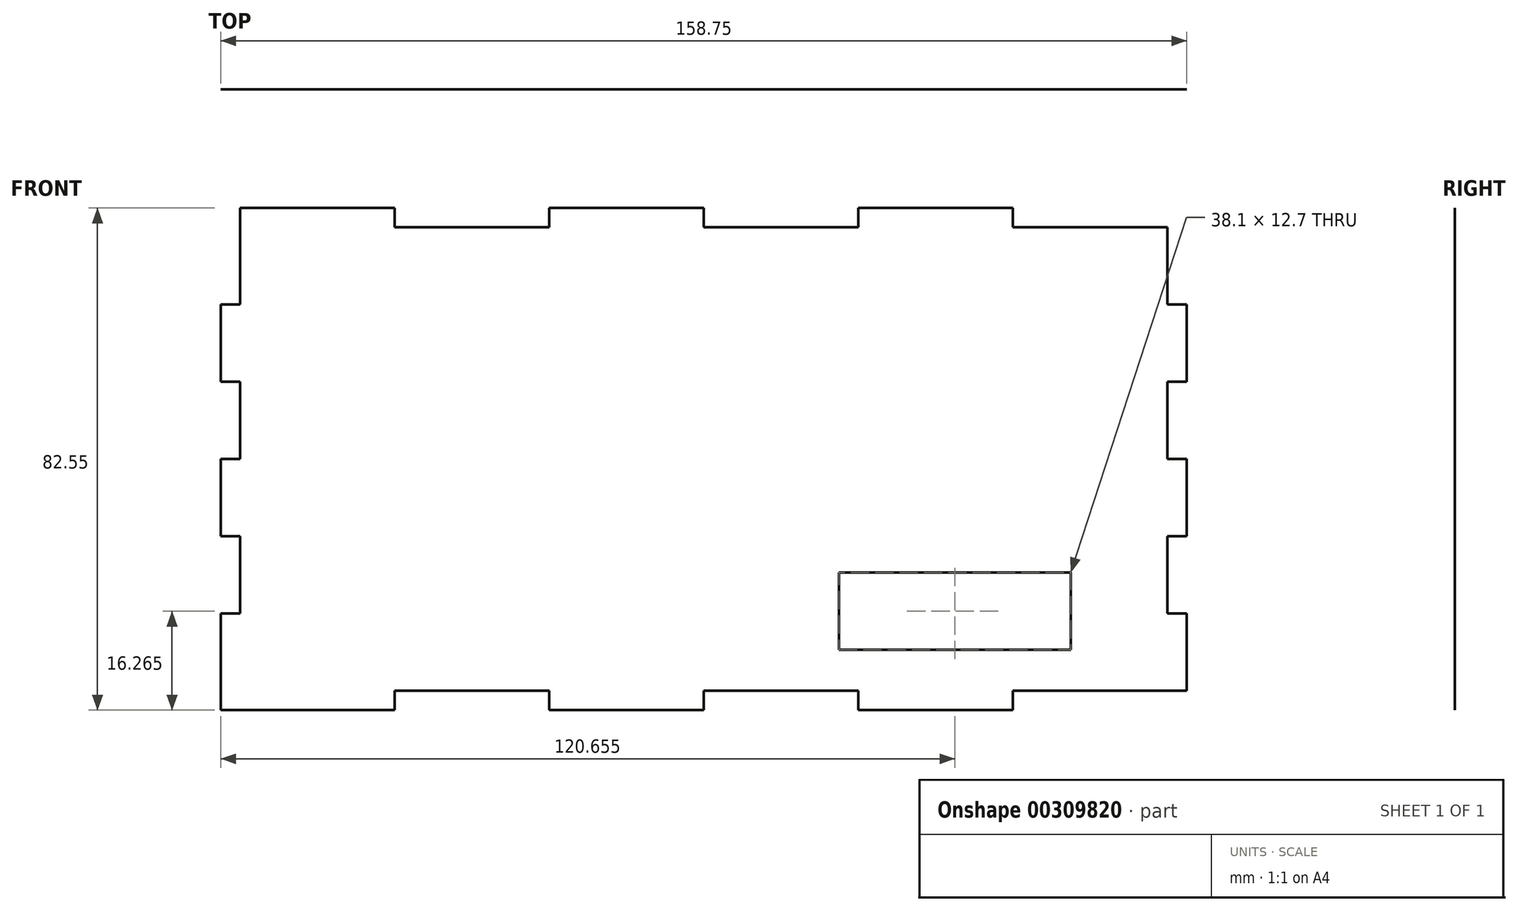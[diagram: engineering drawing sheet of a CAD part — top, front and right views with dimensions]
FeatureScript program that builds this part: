
annotation { "Feature Type Name" : "Feature", "Feature Type Description" : "" }
export const myFeature = defineFeature(function(context is Context, id is Id, definition is map)
    precondition{}
    {
        {
            var Q0;
            Q0=qCreatedBy(makeId("Front.planeOp"),FACE);
            var sketch = newSketch(context, id + "F0", { "sketchPlane" : qUnion([Q0])});
            skLineSegment(sketch, "E0.0.27", {"start": v(15.28, 6.96) * mm, "end": v(-10.12, 6.96) * mm});
            skLineSegment(sketch, "E0.0.28", {"start": v(-10.12, 6.96) * mm, "end": v(-10.12, 10.13) * mm});
            skLineSegment(sketch, "E0.0.29", {"start": v(-10.12, 10.13) * mm, "end": v(-35.52, 10.13) * mm});
            skLineSegment(sketch, "E0.0.30", {"start": v(-35.52, 10.13) * mm, "end": v(-35.52, 6.96) * mm});
            skLineSegment(sketch, "E0.0.31", {"start": v(-35.52, 6.96) * mm, "end": v(-60.92, 6.96) * mm});
            skLineSegment(sketch, "E0.0.32", {"start": v(-60.92, 6.96) * mm, "end": v(-60.92, 10.13) * mm});
            skLineSegment(sketch, "E0.0.33", {"start": v(-60.92, 10.13) * mm, "end": v(-86.32, 10.13) * mm});
            skLineSegment(sketch, "E0.0.34", {"start": v(-86.32, 10.13) * mm, "end": v(-86.32, 6.96) * mm});
            skLineSegment(sketch, "E0.0.35", {"start": v(-86.32, 6.96) * mm, "end": v(-111.72, 6.96) * mm});
            skLineSegment(sketch, "E0.0.36", {"start": v(-111.72, 6.96) * mm, "end": v(-111.72, 10.13) * mm});
            skLineSegment(sketch, "E0.0.37", {"start": v(-111.72, 10.13) * mm, "end": v(-137.12, 10.13) * mm});
            skLineSegment(sketch, "E0.0.38", {"start": v(-137.12, 10.13) * mm, "end": v(-137.12, 6.96) * mm});
            skLineSegment(sketch, "E0.0.41", {"start": v(-140.3, -5.74) * mm, "end": v(-137.12, -5.74) * mm});
            skLineSegment(sketch, "E0.0.43", {"start": v(-137.12, -18.44) * mm, "end": v(-140.3, -18.44) * mm});
            skLineSegment(sketch, "E0.0.45", {"start": v(-140.3, -31.14) * mm, "end": v(-137.12, -31.14) * mm});
            skLineSegment(sketch, "E0.0.47", {"start": v(-137.12, -43.84) * mm, "end": v(-140.3, -43.84) * mm});
            skLineSegment(sketch, "E0.0.49", {"start": v(-140.3, -56.54) * mm, "end": v(-137.12, -56.54) * mm});
            skLineSegment(sketch, "E0.0.51", {"start": v(-137.12, -72.42) * mm, "end": v(-111.72, -72.42) * mm});
            skLineSegment(sketch, "E0.0.52", {"start": v(-111.72, -72.42) * mm, "end": v(-111.72, -69.24) * mm});
            skLineSegment(sketch, "E0.0.53", {"start": v(-111.72, -69.24) * mm, "end": v(-86.32, -69.24) * mm});
            skLineSegment(sketch, "E0.0.54", {"start": v(-86.32, -69.24) * mm, "end": v(-86.32, -72.42) * mm});
            skLineSegment(sketch, "E0.0.55", {"start": v(-86.32, -72.42) * mm, "end": v(-60.92, -72.42) * mm});
            skLineSegment(sketch, "E0.0.56", {"start": v(-60.92, -72.42) * mm, "end": v(-60.92, -69.24) * mm});
            skLineSegment(sketch, "E0.0.57", {"start": v(-60.92, -69.24) * mm, "end": v(-35.52, -69.24) * mm});
            skLineSegment(sketch, "E0.0.58", {"start": v(-35.52, -69.24) * mm, "end": v(-35.52, -72.42) * mm});
            skLineSegment(sketch, "E0.0.59", {"start": v(-35.52, -72.42) * mm, "end": v(-10.12, -72.42) * mm});
            skLineSegment(sketch, "E0.0.60", {"start": v(-10.12, -72.42) * mm, "end": v(-10.12, -69.24) * mm});
            skLineSegment(sketch, "E0.0.61", {"start": v(-10.12, -69.24) * mm, "end": v(15.28, -69.24) * mm});
            skLineSegment(sketch, "E1", {"start": v(-137.12, 6.96) * mm, "end": v(-137.12, -5.74) * mm});
            skLineSegment(sketch, "E2", {"start": v(-140.3, -5.74) * mm, "end": v(-140.3, -18.44) * mm});
            skLineSegment(sketch, "E3", {"start": v(-137.12, -18.44) * mm, "end": v(-137.12, -31.14) * mm});
            skLineSegment(sketch, "E4", {"start": v(-140.3, -31.14) * mm, "end": v(-140.3, -43.84) * mm});
            skLineSegment(sketch, "E5", {"start": v(-137.12, -43.84) * mm, "end": v(-137.12, -56.54) * mm});
            skLineSegment(sketch, "E6", {"start": v(-140.3, -69.24) * mm, "end": v(-140.3, -56.54) * mm});
            skLineSegment(sketch, "E7", {"start": v(15.28, 6.96) * mm, "end": v(15.28, -5.74) * mm});
            skLineSegment(sketch, "E8.MirrorCS", {"start": v(18.45, -5.74) * mm, "end": v(18.45, -18.44) * mm});
            skLineSegment(sketch, "E9.MirrorCS", {"start": v(18.45, -31.14) * mm, "end": v(18.45, -43.84) * mm});
            skLineSegment(sketch, "E10.MirrorCS", {"start": v(18.45, -69.24) * mm, "end": v(18.45, -56.54) * mm});
            skLineSegment(sketch, "E11.MirrorCS", {"start": v(15.28, -69.24) * mm, "end": v(18.45, -69.24) * mm});
            skLineSegment(sketch, "E12.MirrorCS", {"start": v(18.45, -56.54) * mm, "end": v(15.28, -56.54) * mm});
            skLineSegment(sketch, "E13.MirrorCS", {"start": v(15.28, -43.84) * mm, "end": v(18.45, -43.84) * mm});
            skLineSegment(sketch, "E14.MirrorCS", {"start": v(18.45, -31.14) * mm, "end": v(15.28, -31.14) * mm});
            skLineSegment(sketch, "E15.MirrorCS", {"start": v(15.28, -18.44) * mm, "end": v(18.45, -18.44) * mm});
            skLineSegment(sketch, "E16.MirrorCS", {"start": v(18.45, -5.74) * mm, "end": v(15.28, -5.74) * mm});
            skLineSegment(sketch, "E17.trimOffspring", {"start": v(15.28, -18.44) * mm, "end": v(15.28, -31.14) * mm});
            skLineSegment(sketch, "E18.trimOffspring", {"start": v(15.28, -43.84) * mm, "end": v(15.28, -56.54) * mm});
            skLineSegment(sketch, "E19", {"start": v(-137.12, -72.42) * mm, "end": v(-140.3, -72.42) * mm});
            skLineSegment(sketch, "E20", {"start": v(-140.3, -72.42) * mm, "end": v(-140.3, -69.24) * mm});
            skPoint(sketch, "E21.end.orphan", {"position": v(-137.12, -69.24) * mm});
            skSolve(sketch);
        }
        {
            var Q0;
            Q0=makeQuery(id+"F0.imprint","IMPRINT",FACE,{"disambiguationData":[TD([[makeQuery(id+"F0.imprint","IMPRINT",EDGE,{"derivedFrom":sQuery(id+"F0.wireOp",EDGE,"E0.0.27")}),1.0]])]});
            extrude(context, id + "F1", {"entities" : qUnion([Q0]), "depth" : 1 / 203.2 * mm});
        }
        {
            var Q0;
            Q0=makeQuery(id+"F1.opExtrude","CAP_FACE",FACE,{"disambiguationData":[OSD([sQuery(id+"F0.wireOp",EDGE,"E0.0.27"),sQuery(id+"F0.wireOp",EDGE,"E0.0.28"),sQuery(id+"F0.wireOp",EDGE,"E0.0.29"),sQuery(id+"F0.wireOp",EDGE,"E0.0.30"),sQuery(id+"F0.wireOp",EDGE,"E0.0.31"),sQuery(id+"F0.wireOp",EDGE,"E0.0.32"),sQuery(id+"F0.wireOp",EDGE,"E0.0.33"),sQuery(id+"F0.wireOp",EDGE,"E0.0.34"),sQuery(id+"F0.wireOp",EDGE,"E0.0.35"),sQuery(id+"F0.wireOp",EDGE,"E0.0.36"),sQuery(id+"F0.wireOp",EDGE,"E0.0.37"),sQuery(id+"F0.wireOp",EDGE,"E0.0.38"),sQuery(id+"F0.wireOp",EDGE,"E0.0.41"),sQuery(id+"F0.wireOp",EDGE,"E0.0.43"),sQuery(id+"F0.wireOp",EDGE,"E0.0.45"),sQuery(id+"F0.wireOp",EDGE,"E0.0.47"),sQuery(id+"F0.wireOp",EDGE,"E0.0.49"),sQuery(id+"F0.wireOp",EDGE,"E0.0.51"),sQuery(id+"F0.wireOp",EDGE,"E0.0.52"),sQuery(id+"F0.wireOp",EDGE,"E0.0.53"),sQuery(id+"F0.wireOp",EDGE,"E0.0.54"),sQuery(id+"F0.wireOp",EDGE,"E0.0.55"),sQuery(id+"F0.wireOp",EDGE,"E0.0.56"),sQuery(id+"F0.wireOp",EDGE,"E0.0.57"),sQuery(id+"F0.wireOp",EDGE,"E0.0.58"),sQuery(id+"F0.wireOp",EDGE,"E0.0.59"),sQuery(id+"F0.wireOp",EDGE,"E0.0.60"),sQuery(id+"F0.wireOp",EDGE,"E0.0.61"),sQuery(id+"F0.wireOp",EDGE,"E1"),sQuery(id+"F0.wireOp",EDGE,"E2"),sQuery(id+"F0.wireOp",EDGE,"E3"),sQuery(id+"F0.wireOp",EDGE,"E4"),sQuery(id+"F0.wireOp",EDGE,"E5"),sQuery(id+"F0.wireOp",EDGE,"E6"),sQuery(id+"F0.wireOp",EDGE,"E7"),sQuery(id+"F0.wireOp",EDGE,"E8.MirrorCS"),sQuery(id+"F0.wireOp",EDGE,"E9.MirrorCS"),sQuery(id+"F0.wireOp",EDGE,"E10.MirrorCS"),sQuery(id+"F0.wireOp",EDGE,"E11.MirrorCS"),sQuery(id+"F0.wireOp",EDGE,"E12.MirrorCS"),sQuery(id+"F0.wireOp",EDGE,"E13.MirrorCS"),sQuery(id+"F0.wireOp",EDGE,"E14.MirrorCS"),sQuery(id+"F0.wireOp",EDGE,"E15.MirrorCS"),sQuery(id+"F0.wireOp",EDGE,"E16.MirrorCS"),sQuery(id+"F0.wireOp",EDGE,"E17.trimOffspring"),sQuery(id+"F0.wireOp",EDGE,"E18.trimOffspring"),sQuery(id+"F0.wireOp",EDGE,"E19"),sQuery(id+"F0.wireOp",EDGE,"E20")])],"isStart":false});
            var sketch = newSketch(context, id + "F2", { "sketchPlane" : qUnion([Q0])});
            skLineSegment(sketch, "E22.bottom", {"start": v(-38.7, -49.8) * mm, "end": v(-0.6, -49.8) * mm});
            skLineSegment(sketch, "E22.top", {"start": v(-38.7, -62.5) * mm, "end": v(-0.6, -62.5) * mm});
            skLineSegment(sketch, "E22.left", {"start": v(-38.7, -49.8) * mm, "end": v(-38.7, -62.5) * mm});
            skLineSegment(sketch, "E22.right", {"start": v(-0.6, -49.8) * mm, "end": v(-0.6, -62.5) * mm});
            skSolve(sketch);
        }
        {
            var Q0;
            Q0=makeQuery(id+"F2.imprint","IMPRINT",FACE,{"disambiguationData":[TD([[makeQuery(id+"F2.imprint","IMPRINT",EDGE,{"derivedFrom":sQuery(id+"F2.wireOp",EDGE,"E22.bottom")}),-1.0]])]});
            extrude(context, id + "F3", {"entities" : qUnion([Q0]), "operationType" : NewBodyOperationType.REMOVE, "oppositeDirection" : true, "depth" : 25.4 * mm});
        }
    });
